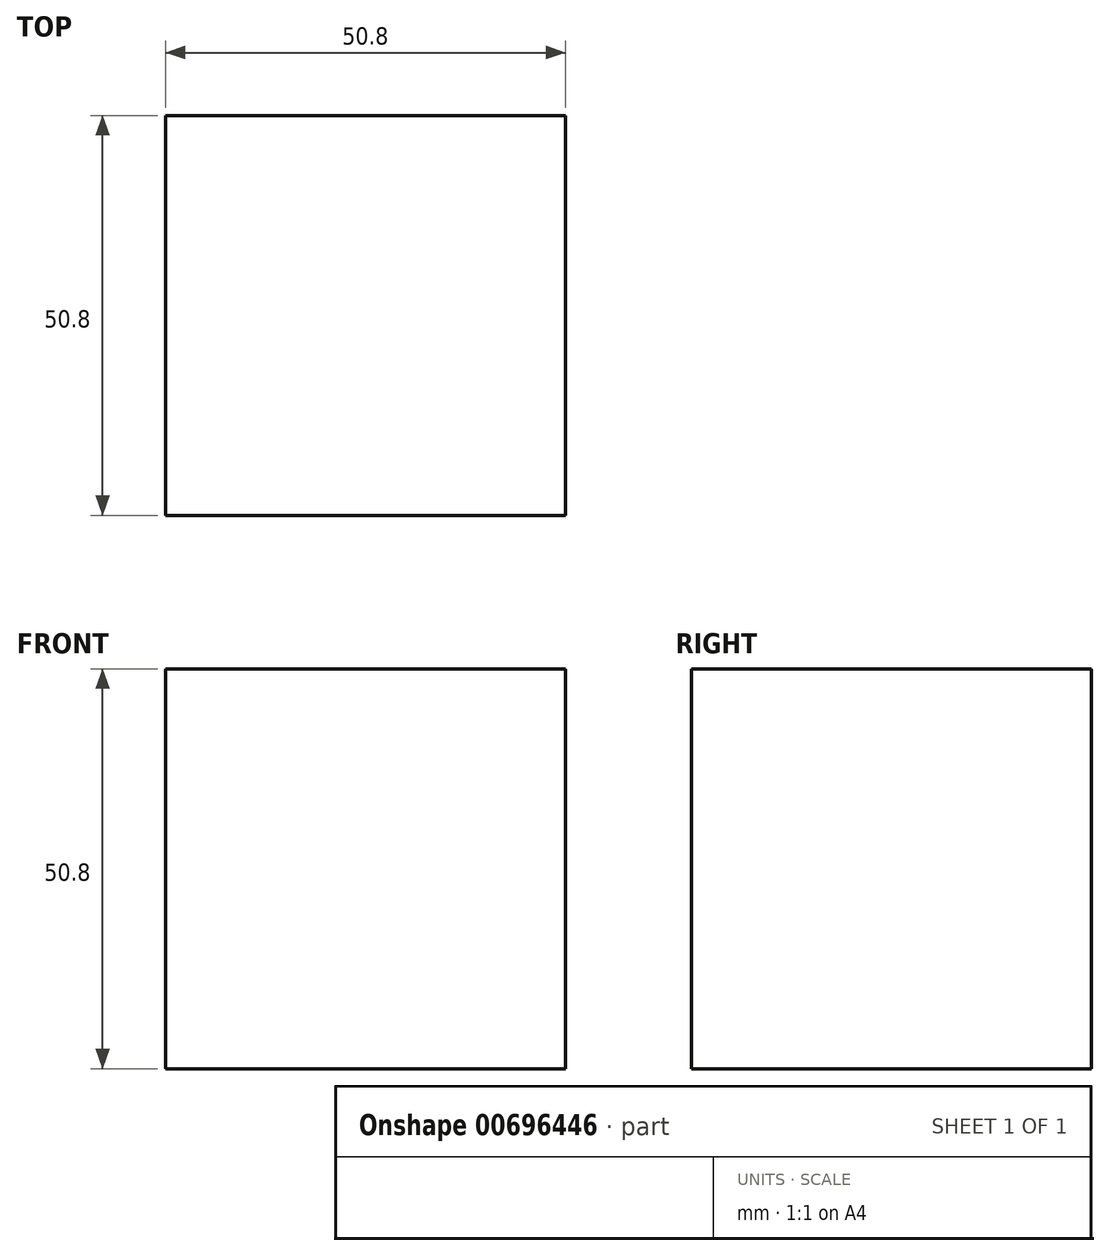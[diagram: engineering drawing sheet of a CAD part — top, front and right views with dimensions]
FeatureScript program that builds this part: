
annotation { "Feature Type Name" : "Feature", "Feature Type Description" : "" }
export const myFeature = defineFeature(function(context is Context, id is Id, definition is map)
    precondition{}
    {
        {
            var Q0;
            Q0=qCreatedBy(makeId("Front.planeOp"),FACE);
            var sketch = newSketch(context, id + "F0", { "sketchPlane" : qUnion([Q0])});
            skLineSegment(sketch, "E0.bottom", {"start": v(-29.5, 15.76) * mm, "end": v(21.3, 15.76) * mm});
            skLineSegment(sketch, "E0.top", {"start": v(-29.5, -35.04) * mm, "end": v(21.3, -35.04) * mm});
            skLineSegment(sketch, "E0.left", {"start": v(-29.5, 15.76) * mm, "end": v(-29.5, -35.04) * mm});
            skLineSegment(sketch, "E0.right", {"start": v(21.3, 15.76) * mm, "end": v(21.3, -35.04) * mm});
            skLineSegment(sketch, "E1", {"start": v(0, 0) * mm, "end": v(0, 15.76) * mm});
            skLineSegment(sketch, "E2", {"start": v(0, 0) * mm, "end": v(-29.5, 0) * mm});
            skSolve(sketch);
        }
        {
            var Q0;
            Q0 = qSketchRegion(id + "F0", true);
            extrude(context, id + "F1", {"entities" : qUnion([Q0]), "depth" : 50.8 * mm, "offsetDistance" : 25.4 * mm});
        }
    });
